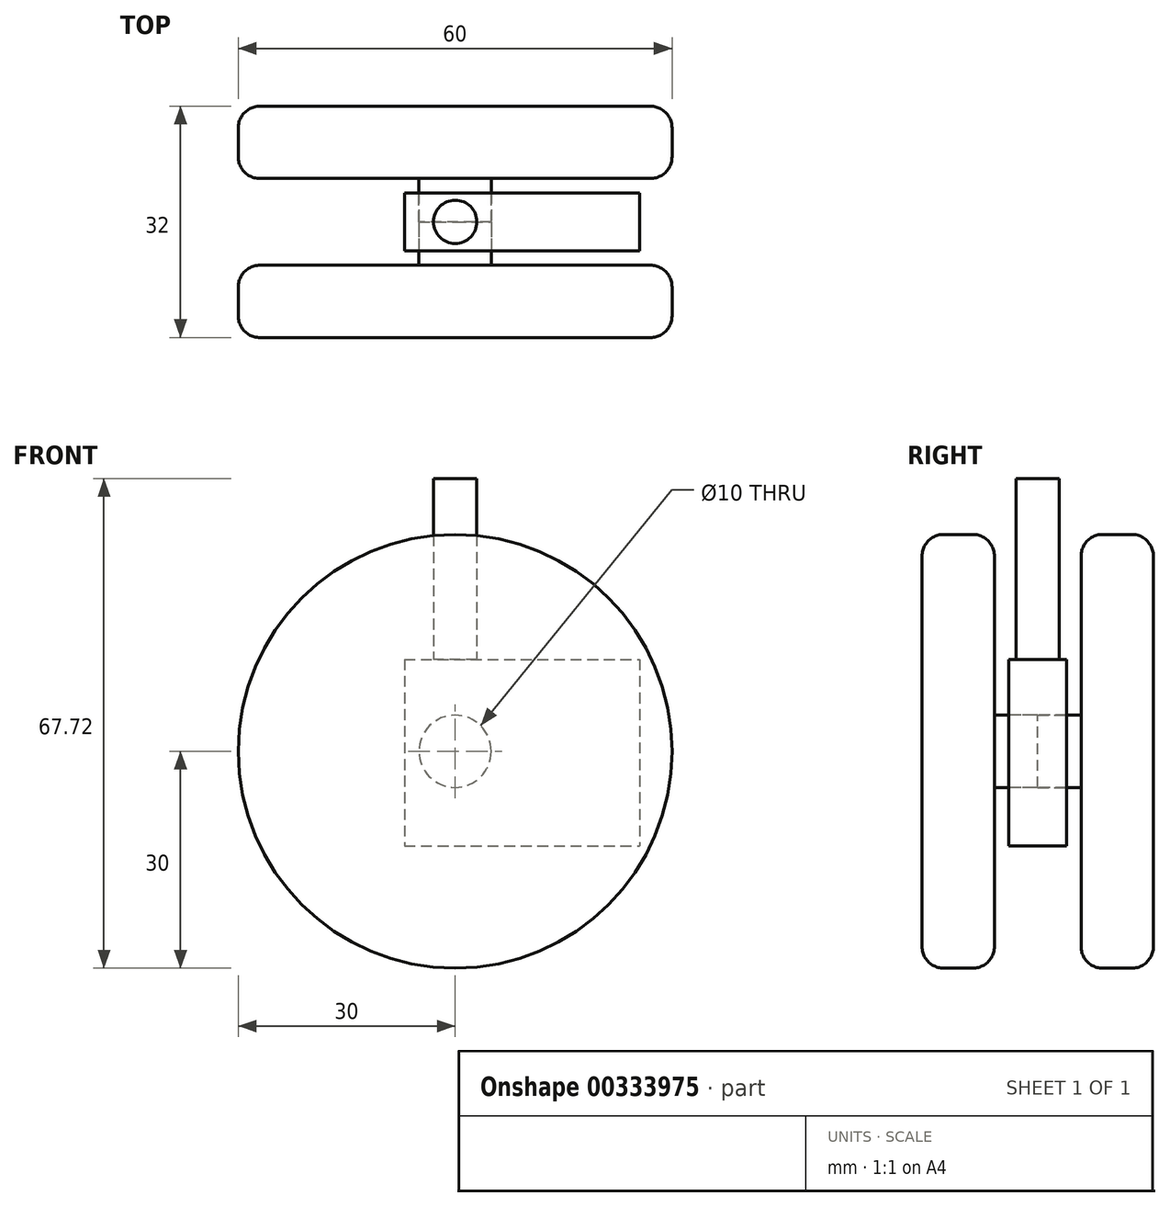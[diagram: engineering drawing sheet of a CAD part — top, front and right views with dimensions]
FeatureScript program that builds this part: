
annotation { "Feature Type Name" : "Feature", "Feature Type Description" : "" }
export const myFeature = defineFeature(function(context is Context, id is Id, definition is map)
    precondition{}
    {
        {
            var Q0;
            Q0=qCreatedBy(makeId("Front.planeOp"),FACE);
            var sketch = newSketch(context, id + "F0", { "sketchPlane" : qUnion([Q0])});
            skCircle(sketch, "E0", {"center": v(0, 0) * mm, "radius": 30 * mm});
            skSolve(sketch);
        }
        {
            var Q0;
            Q0=makeQuery(id+"F0.imprint","IMPRINT",FACE,{"disambiguationData":[TD([[makeQuery(id+"F0.imprint","IMPRINT",EDGE,{"derivedFrom":sQuery(id+"F0.wireOp",EDGE,"E0")}),1.0]])]});
            extrude(context, id + "F1", {"entities" : qUnion([Q0]), "depth" : 10 * mm});
        }
        {
            var Q0;
            Q0=makeQuery(id+"F1.opExtrude","CAP_FACE",FACE,{"disambiguationData":[OSD([sQuery(id+"F0.wireOp",EDGE,"E0")])],"isStart":false});
            var Q1;
            Q1=makeQuery(id+"F1.opExtrude","CAP_FACE",FACE,{"disambiguationData":[OSD([sQuery(id+"F0.wireOp",EDGE,"E0")])],"isStart":true});
            fillet(context, id + "F2", {"entities" : qUnion([Q0, Q1]), "radius" : 3 * mm, "tangentPropagation" : true, "allowEdgeOverflow" : false});
        }
        {
            var Q0;
            Q0=qCreatedBy(makeId("Front.planeOp"),FACE);
            var sketch = newSketch(context, id + "F3", { "sketchPlane" : qUnion([Q0])});
            skCircle(sketch, "E1", {"center": v(0, 0) * mm, "radius": 5 * mm});
            skSolve(sketch);
        }
        {
            var Q0;
            Q0 = qSketchRegion(id + "F3", true);
            extrude(context, id + "F4", {"entities" : qUnion([Q0]), "operationType" : NewBodyOperationType.ADD, "oppositeDirection" : true, "depth" : 6 * mm});
        }
        {
            var Q0;
            Q0=makeQuery(id+"F1.opExtrude","SWEPT_BODY",BODY,{"disambiguationData":[OSD([sQuery(id+"F0.wireOp",EDGE,"E0")])]});
            var Q1;
            Q1=makeQuery(id+"F4.opExtrude","CAP_FACE",FACE,{"disambiguationData":[OSD([sQuery(id+"F3.wireOp",EDGE,"E1")])],"isStart":false});
            mirror(context, id + "F5", {"entities" : qUnion([Q0]), "mirrorPlane" : qUnion([Q1])});
        }
        {
            var Q0;
            Q0=makeQuery(id+"F4.opExtrude","CAP_FACE",FACE,{"disambiguationData":[OSD([sQuery(id+"F3.wireOp",EDGE,"E1")])],"isStart":false});
            var sketch = newSketch(context, id + "F6", { "sketchPlane" : qUnion([Q0])});
            skLineSegment(sketch, "E2.bottom", {"start": v(7.02, 12.72) * mm, "end": v(-25.53, 12.72) * mm});
            skLineSegment(sketch, "E2.top", {"start": v(7.02, -13.1) * mm, "end": v(-25.53, -13.1) * mm});
            skLineSegment(sketch, "E2.left", {"start": v(7.02, 12.72) * mm, "end": v(7.02, -13.1) * mm});
            skLineSegment(sketch, "E2.right", {"start": v(-25.53, 12.72) * mm, "end": v(-25.53, -13.1) * mm});
            skSolve(sketch);
        }
        {
            var Q0;
            Q0=makeQuery(id+"F6.imprint","IMPRINT",FACE,{"disambiguationData":[TD([[makeQuery(id+"F6.imprint","IMPRINT",EDGE,{"derivedFrom":sQuery(id+"F6.wireOp",EDGE,"E2.bottom")}),1.0]])]});
            extrude(context, id + "F7", {"entities" : qUnion([Q0]), "endBound" : BoundingType.SYMMETRIC, "depth" : 8 * mm});
        }
        {
            var Q0;
            Q0=makeQuery(id+"F7.opExtrude","SWEPT_FACE",FACE,{"disambiguationData":[OSD([sQuery(id+"F6.wireOp",EDGE,"E2.bottom")])]});
            var sketch = newSketch(context, id + "F8", { "sketchPlane" : qUnion([Q0])});
            skLineSegment(sketch, "E3", {"start": v(0, 10) * mm, "end": v(0, 2) * mm, "construction": true});
            skCircle(sketch, "E4", {"center": v(0, 6) * mm, "radius": 3 * mm});
            skSolve(sketch);
        }
        {
            var Q0;
            Q0 = qSketchRegion(id + "F8", true);
            extrude(context, id + "F9", {"entities" : qUnion([Q0]), "operationType" : NewBodyOperationType.ADD, "depth" : 25 * mm});
        }
        {
            var Q0;
            Q0=makeQuery(id+"F1.opExtrude","SWEPT_BODY",BODY,{"disambiguationData":[OSD([sQuery(id+"F0.wireOp",EDGE,"E0")])]});
            var Q1;
            Q1=makeQuery(id+"F7.opExtrude","SWEPT_BODY",BODY,{"disambiguationData":[OSD([sQuery(id+"F3.wireOp",EDGE,"E1"),sQuery(id+"F6.wireOp",EDGE,"E2.bottom"),sQuery(id+"F6.wireOp",EDGE,"E2.top"),sQuery(id+"F6.wireOp",EDGE,"E2.left"),sQuery(id+"F6.wireOp",EDGE,"E2.right")])]});
            var Q2;
            Q2=makeQuery(id+"F5.opPattern","COPY",BODY,{"derivedFrom":makeQuery(id+"F1.opExtrude","SWEPT_BODY",BODY,{"disambiguationData":[OSD([sQuery(id+"F0.wireOp",EDGE,"E0")])]}),"instanceName":"1"});
            var Q3;
            Q3=qCreatedBy(makeId("Front.planeOp"),FACE);
            transform(context, id + "F10", {"entities" : qUnion([Q0, Q1, Q2]), "transformType" : TransformType.TRANSLATION_DISTANCE, "transformDirection" : qUnion([Q3]), "distance" : 6 * mm, "makeCopy" : false});
        }
    });
